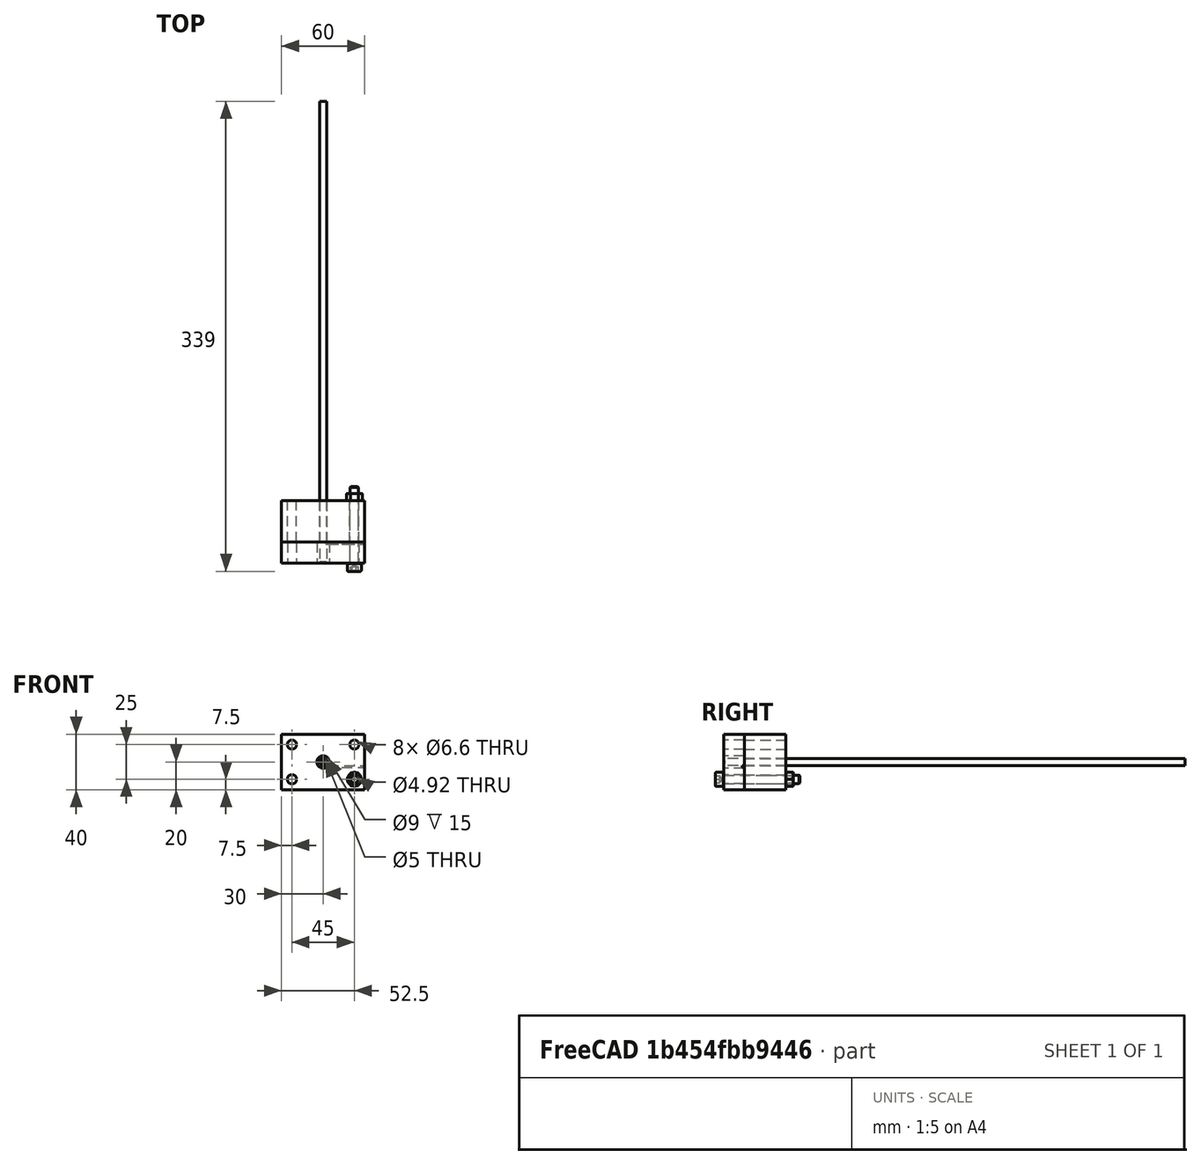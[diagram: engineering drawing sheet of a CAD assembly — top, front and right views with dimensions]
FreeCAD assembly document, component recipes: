
FREECAD ASSEMBLY — COMPONENT RECIPES ("coil winder")

This assembly document has 4 components, labeled P0..P3 below (a component is one placed body or linked part). 3 of them carry a construction recipe — the FreeCAD feature program that regenerates the part from scratch, quoted from this document or its linked companion documents; the rest are supplied as boundary geometry only. No exploded tour is included for this assembly.
COMPONENT P0 — geometry summary ("block fasteners"; no construction recipe available for this part):
  bounding box: 61.0 x 56.5 x 35.0 mm
  tessellated surface: 35,832 triangles
  volume: 9135 mm^3 (8% of its bounding box)
  symmetry: 2-fold rotationally symmetric about the y axis; mirror-symmetric across its x mid-plane, z mid-plane
COMPONENT P1 — recipe-attached ("OCT-CWFBL-AA", modeled in this document).
Construction recipe (the document's own serialized feature program — sketch geometry with constraints, then the solid features built on it; lengths are millimeters unless a unit is written):

FEATURE [PartDesign::SubShapeBinder] Binder  label="rear block binder"
  BindCopyOnChange = 0
  BindMode = 0
  ClaimChildren = false
  Context = -> Body001 [Binder.]
  Fuse = false
  MakeFace = true
  OffsetFill = false
  OffsetIntersection = false
  OffsetJoinType = 0
  OffsetOpenResult = false
  PartialLoad = false
  Refine = true
  Relative = true
  Support = -> [Body[Hole002.]]
  _Version = 2
FEATURE [Sketcher::SketchObject] Sketch002
  ArcFitTolerance = 1e-06
  AttachmentSupport = -> [XZ_Plane001]
  ExternalGeometry = -> [Binder]
  FullyConstrained = true
  MakeInternals = false
  MapMode = 5
  Placement = pos=(0,0,0) rot=(1,0,0;1.5708rad)
  sketch-geometry (4):
    g0: LineSegment StartX=-30 StartY=0 StartZ=0 EndX=30 EndY=0 EndZ=0
    g1: LineSegment StartX=30 StartY=0 StartZ=0 EndX=30 EndY=40 EndZ=0
    g2: LineSegment StartX=30 StartY=40 StartZ=0 EndX=-30 EndY=40 EndZ=0
    g3: LineSegment StartX=-30 StartY=40 StartZ=0 EndX=-30 EndY=0 EndZ=0
  constraints (10):
    c: Coincident(g0,g1)
    c: Coincident(g1,g2)
    c: Coincident(g2,g3)
    c: Coincident(g3,g0)
    c: Horizontal(g2)
    c: Vertical(g1)
    c: Vertical(g3)
    c: PointOnObject(g0,g-1)
    c: Coincident(g2,g-3)
    c: Symmetric(g0,g0,g-2)
FEATURE [PartDesign::Pad] Pad001
  Direction = (0,-1,2e-16)
  Length = 15
  Length2 = 10
  Placement = pos=(0,0,0) rot=(1,0,0;1.5708rad)
  Profile = -> Sketch002
  ReferenceAxis = -> Sketch002 [N_Axis]
  Refine = true
  Suppressed = false
  Type = 0
FEATURE [Sketcher::SketchObject] Sketch003
  ArcFitTolerance = 1e-06
  AttachmentSupport = -> [XZ_Plane001]
  ExternalGeometry = -> [Binder]
  FullyConstrained = true
  MakeInternals = false
  MapMode = 5
  Placement = pos=(0,0,0) rot=(1,0,0;1.5708rad)
  expr: Constraints[0] = <<dims>>.shaftDiameter + 2 * <<dims>>.wireDiameter
  sketch-geometry (1):
    g0: Circle CenterX=0 CenterY=20 CenterZ=0 NormalX=0 NormalY=0 NormalZ=1 AngleXU=0 Radius=3.52
  constraints (2):
    c: Diameter(g0) = 7.04
    c: Coincident(g0,g-3)
FEATURE [PartDesign::Hole] Hole001  label="coil bore"
  BaseFeature = -> Pad001
  CustomThreadClearance = 0
  Depth = 148.782
  DepthType = 1
  Diameter = 9
  DrillForDepth = false
  DrillPoint = 1
  DrillPointAngle = 118
  HoleCutCountersinkAngle = 90
  HoleCutCustomValues = false
  HoleCutDepth = 0
  HoleCutDiameter = 6.1
  HoleCutType = 0
  ModelThread = false
  Placement = pos=(0,0,0) rot=(1,0,0;1.5708rad)
  Profile = -> Sketch003
  Refine = true
  Reversed = true
  Suppressed = false
  Tapered = false
  TaperedAngle = 90
  ThreadClass = 0
  ThreadDepth = 148.782
  ThreadDepthType = 0
  ThreadDirection = 0
  ThreadFit = 0
  ThreadSize = 0
  ThreadType = 0
  Threaded = false
  UseCustomThreadClearance = false
  expr: Diameter = ceil(<<dims>>.shaftDiameter + 2 * <<dims>>.wireDiameter) + 1 mm
FEATURE [Sketcher::SketchObject] Sketch004
  ArcFitTolerance = 1e-06
  AttachmentSupport = -> [YZ_Plane001]
  ExternalGeometry = -> [Hole001]
  FullyConstrained = true
  MakeInternals = false
  MapMode = 5
  Placement = pos=(0,0,0) rot=(0.57735,0.57735,0.57735;2.0944rad)
  expr: Constraints[17] = <<dims>>.shaftDiameter / 2
  expr: Constraints[8] = <<dims>>.wireDiameter + 0.5 mm
  sketch-geometry (8):
    g0: LineSegment StartX=-1.52 StartY=15.98 StartZ=0 EndX=4e-15 EndY=15.98 EndZ=0
    g1: LineSegment StartX=4e-15 StartY=15.98 StartZ=0 EndX=4e-15 EndY=17.5 EndZ=0
    g2: LineSegment StartX=4e-15 StartY=17.5 StartZ=0 EndX=-1.52 EndY=17.5 EndZ=0
    g3: LineSegment StartX=-1.52 StartY=17.5 StartZ=0 EndX=-1.52 EndY=15.98 EndZ=0
    g4: LineSegment [constr] StartX=-1.52 StartY=17.5 StartZ=0 EndX=4e-15 EndY=15.98 EndZ=0
    g5: LineSegment [constr] StartX=-1.52 StartY=15.98 StartZ=0 EndX=4e-15 EndY=17.5 EndZ=0
    g6: GeomPoint [constr] X=-0.76 Y=16.74 Z=0
    g7: GeomPoint [constr] X=4.4e-15 Y=20 Z=0
  constraints (19):
    c: Coincident(g0,g1)
    c: Coincident(g1,g2)
    c: Coincident(g2,g3)
    c: Coincident(g3,g0)
    c: Horizontal(g0)
    c: Horizontal(g2)
    c: Vertical(g1)
    c: Vertical(g3)
    c: DistanceY(g3,g3) = 1.52
    c: Coincident(g4,g2)
    c: Coincident(g4,g0)
    c: Coincident(g5,g0)
    c: Coincident(g5,g1)
    c: PointOnObject(g6,g4)
    c: PointOnObject(g6,g5)
    c: Equal(g3,g0)
    c: Symmetric(g-3,g-3,g7)
    c: DistanceY(g1,g7) = 2.5
    c: PointOnObject(g1,g-3)
FEATURE [PartDesign::Pocket] Pocket  label="wire insert groove"
  BaseFeature = -> Hole001
  Direction = (-1,0,0)
  Length = 5
  Length2 = 5
  Placement = pos=(0,0,0) rot=(1,0,0;1.5708rad)
  Profile = -> Sketch004
  ReferenceAxis = -> Sketch004 [N_Axis]
  Refine = true
  Reversed = true
  Suppressed = false
  Type = 1
FEATURE [Sketcher::SketchObject] Sketch006
  ArcFitTolerance = 1e-06
  AttachmentSupport = -> [XZ_Plane001]
  FullyConstrained = true
  MakeInternals = false
  MapMode = 5
  Placement = pos=(0,0,0) rot=(1,0,0;1.5708rad)
  expr: Constraints[18] = <<dims>>.holeSpacingX
  expr: Constraints[19] = <<dims>>.holeSpacingZ
  expr: Constraints[20] = <<dims>>.shaftZ
  sketch-geometry (9):
    g0: LineSegment [constr] StartX=-22.5 StartY=7.5 StartZ=0 EndX=22.5 EndY=7.5 EndZ=0
    g1: LineSegment [constr] StartX=22.5 StartY=7.5 StartZ=0 EndX=22.5 EndY=32.5 EndZ=0
    g2: LineSegment [constr] StartX=22.5 StartY=32.5 StartZ=0 EndX=-22.5 EndY=32.5 EndZ=0
    g3: LineSegment [constr] StartX=-22.5 StartY=32.5 StartZ=0 EndX=-22.5 EndY=7.5 EndZ=0
    g4: GeomPoint [constr] X=0 Y=20 Z=0
    g5: Circle CenterX=-22.5 CenterY=32.5 CenterZ=0 NormalX=0 NormalY=0 NormalZ=1 AngleXU=0 Radius=3
    g6: Circle CenterX=22.5 CenterY=32.5 CenterZ=0 NormalX=0 NormalY=0 NormalZ=1 AngleXU=0 Radius=3
    g7: Circle CenterX=22.5 CenterY=7.5 CenterZ=0 NormalX=0 NormalY=0 NormalZ=1 AngleXU=0 Radius=3
    g8: Circle CenterX=-22.5 CenterY=7.5 CenterZ=0 NormalX=0 NormalY=0 NormalZ=1 AngleXU=0 Radius=3
  constraints (21):
    c: Coincident(g0,g1)
    c: Coincident(g1,g2)
    c: Coincident(g2,g3)
    c: Coincident(g3,g0)
    c: Horizontal(g0)
    c: Horizontal(g2)
    c: Vertical(g1)
    c: Vertical(g3)
    c: Symmetric(g2,g0,g4)
    c: PointOnObject(g4,g-2)
    c: Coincident(g5,g2)
    c: Coincident(g6,g1)
    c: Coincident(g7,g0)
    c: Coincident(g8,g0)
    c: Equal(g8,g5)
    c: Equal(g5,g6)
    c: Equal(g6,g7)
    c: Diameter(g5) = 6
    c: DistanceX(g2,g2) = 45
    c: DistanceY(g3,g3) = 25
    c: DistanceY(g-1,g4) = 20
FEATURE [PartDesign::Hole] Hole003  label="bolt holes"
  BaseFeature = -> Pocket
  CustomThreadClearance = 0
  Depth = 148.782
  DepthType = 1
  Diameter = 6.6
  DrillForDepth = false
  DrillPoint = 1
  DrillPointAngle = 118
  HoleCutCountersinkAngle = 90
  HoleCutCustomValues = false
  HoleCutDepth = 0
  HoleCutDiameter = 6.1
  HoleCutType = 0
  ModelThread = false
  Placement = pos=(0,0,0) rot=(1,0,0;1.5708rad)
  Profile = -> Sketch006
  Refine = true
  Reversed = true
  Suppressed = false
  Tapered = false
  TaperedAngle = 90
  ThreadClass = 0
  ThreadDepth = 148.782
  ThreadDepthType = 0
  ThreadDirection = 0
  ThreadFit = 0
  ThreadSize = 14
  ThreadType = 1
  Threaded = false
  UseCustomThreadClearance = false
FEATURE [PartDesign::Body] Body001  label="OCT-CWFBL-AA"
  AllowCompound = false
  Group = -> [Binder,Sketch002,Pad001,Sketch003,Hole001,Sketch004,Pocket,Sketch006,Hole003]
  Origin = -> Origin001
  Tip = -> Hole003
COMPONENT P2 — recipe-attached ("OCT-CWRBL-AA", modeled in this document).
Construction recipe (the document's own serialized feature program — sketch geometry with constraints, then the solid features built on it; lengths are millimeters unless a unit is written):

FEATURE [Sketcher::SketchObject] Sketch  label="block profile"
  ArcFitTolerance = 1e-06
  AttachmentSupport = -> [XZ_Plane]
  FullyConstrained = true
  MakeInternals = false
  MapMode = 5
  Placement = pos=(0,0,0) rot=(1,0,0;1.5708rad)
  expr: Constraints[11] = <<dims>>.shaftDiameter
  sketch-geometry (7):
    g0: LineSegment StartX=-30 StartY=0 StartZ=0 EndX=30 EndY=0 EndZ=0
    g1: LineSegment StartX=30 StartY=0 StartZ=0 EndX=30 EndY=40 EndZ=0
    g2: LineSegment StartX=30 StartY=40 StartZ=0 EndX=-30 EndY=40 EndZ=0
    g3: LineSegment StartX=-30 StartY=40 StartZ=0 EndX=-30 EndY=0 EndZ=0
    g4: Circle [constr] CenterX=0 CenterY=20 CenterZ=0 NormalX=0 NormalY=0 NormalZ=1 AngleXU=0 Radius=2.5
    g5: LineSegment [constr] StartX=2 StartY=18.5 StartZ=0 EndX=30 EndY=18.5 EndZ=0
    g6: GeomPoint [constr] X=0 Y=17.5 Z=0
  constraints (20):
    c: Coincident(g0,g1)
    c: Coincident(g1,g2)
    c: Coincident(g2,g3)
    c: Coincident(g3,g0)
    c: Horizontal(g2)
    c: Vertical(g1)
    c: Vertical(g3)
    c: PointOnObject(g0,g-1)
    c: PointOnObject(g4,g-2)
    c: PointOnObject(g5,g4)
    c: Horizontal(g5)
    c: Diameter(g4) = 5
    c: PointOnObject(g6,g4)
    c: PointOnObject(g6,g-2)
    c: DistanceY(g6,g5) = 1
    c: DistanceY(g-1,g4) = 20
    c: DistanceY(g3,g3) = 40
    c: DistanceX(g2,g2) = 60
    c: Symmetric(g0,g0,g-2)
    c: PointOnObject(g5,g1)
FEATURE [PartDesign::Pad] Pad
  Direction = (0,-1,2e-16)
  Length = 30
  Length2 = 10
  Placement = pos=(0,0,0) rot=(1,0,0;1.5708rad)
  Profile = -> Sketch
  ReferenceAxis = -> Sketch [N_Axis]
  Refine = true
  Reversed = true
  Suppressed = false
  Type = 0
FEATURE [Sketcher::SketchObject] Sketch001
  ArcFitTolerance = 1e-06
  AttachmentSupport = -> [XZ_Plane]
  FullyConstrained = true
  MakeInternals = false
  MapMode = 5
  Placement = pos=(0,0,0) rot=(1,0,0;1.5708rad)
  expr: Constraints[1] = <<dims>>.shaftDiameter
  expr: Constraints[2] = <<dims>>.shaftZ
  sketch-geometry (1):
    g0: Circle CenterX=0 CenterY=20 CenterZ=0 NormalX=0 NormalY=0 NormalZ=1 AngleXU=0 Radius=2.5
  constraints (3):
    c: PointOnObject(g0,g-2)
    c: Diameter(g0) = 5
    c: DistanceY(g-1,g0) = 20
FEATURE [PartDesign::Hole] Hole  label="shaft bore"
  BaseFeature = -> Pad
  CustomThreadClearance = 0
  Depth = 166.573
  DepthType = 1
  Diameter = 5
  DrillForDepth = false
  DrillPoint = 1
  DrillPointAngle = 118
  HoleCutCountersinkAngle = 90
  HoleCutCustomValues = false
  HoleCutDepth = 0
  HoleCutDiameter = 6.1
  HoleCutType = 0
  ModelThread = false
  Placement = pos=(0,0,0) rot=(1,0,0;1.5708rad)
  Profile = -> Sketch001
  Refine = true
  Suppressed = false
  Tapered = false
  TaperedAngle = 90
  ThreadClass = 0
  ThreadDepth = 166.573
  ThreadDepthType = 0
  ThreadDirection = 0
  ThreadFit = 0
  ThreadSize = 0
  ThreadType = 0
  Threaded = false
  UseCustomThreadClearance = false
  expr: Diameter = <<dims>>.shaftDiameter
FEATURE [Sketcher::SketchObject] Sketch005
  ArcFitTolerance = 1e-06
  AttachmentSupport = -> [XZ_Plane]
  ExternalGeometry = -> [Hole]
  FullyConstrained = true
  MakeInternals = false
  MapMode = 5
  Placement = pos=(0,0,0) rot=(1,0,0;1.5708rad)
  expr: Constraints[17] = <<dims>>.holeSpacingX
  expr: Constraints[18] = <<dims>>.holeSpacingZ
  sketch-geometry (9):
    g0: Circle CenterX=-22.5 CenterY=32.5 CenterZ=0 NormalX=0 NormalY=0 NormalZ=1 AngleXU=0 Radius=3
    g1: Circle CenterX=22.5 CenterY=7.5 CenterZ=0 NormalX=0 NormalY=0 NormalZ=1 AngleXU=0 Radius=3
    g2: Circle CenterX=22.5 CenterY=32.5 CenterZ=0 NormalX=0 NormalY=0 NormalZ=1 AngleXU=0 Radius=3
    g3: Circle CenterX=-22.5 CenterY=7.5 CenterZ=0 NormalX=0 NormalY=0 NormalZ=1 AngleXU=0 Radius=3
    g4: LineSegment [constr] StartX=-22.5 StartY=7.5 StartZ=0 EndX=22.5 EndY=7.5 EndZ=0
    g5: LineSegment [constr] StartX=22.5 StartY=7.5 StartZ=0 EndX=22.5 EndY=32.5 EndZ=0
    g6: LineSegment [constr] StartX=22.5 StartY=32.5 StartZ=0 EndX=-22.5 EndY=32.5 EndZ=0
    g7: LineSegment [constr] StartX=-22.5 StartY=32.5 StartZ=0 EndX=-22.5 EndY=7.5 EndZ=0
    g8: GeomPoint [constr] X=-1e-16 Y=20 Z=0
  constraints (20):
    c: Equal(g0,g2)
    c: Equal(g2,g1)
    c: Equal(g1,g3)
    c: Coincident(g4,g5)
    c: Coincident(g5,g6)
    c: Coincident(g6,g7)
    c: Coincident(g7,g4)
    c: Horizontal(g4)
    c: Horizontal(g6)
    c: Vertical(g5)
    c: Vertical(g7)
    c: Symmetric(g6,g4,g8)
    c: Coincident(g8,g-3)
    c: Coincident(g5,g2)
    c: Coincident(g4,g3)
    c: Coincident(g0,g6)
    c: Coincident(g1,g4)
    c: DistanceX(g6,g6) = 45
    c: DistanceY(g7,g7) = 25
    c: Diameter(g0) = 6
FEATURE [PartDesign::Hole] Hole002  label="bolt holes"
  BaseFeature = -> Hole
  CustomThreadClearance = 0
  Depth = 166.573
  DepthType = 1
  Diameter = 6.6
  DrillForDepth = false
  DrillPoint = 1
  DrillPointAngle = 118
  HoleCutCountersinkAngle = 90
  HoleCutCustomValues = false
  HoleCutDepth = 0
  HoleCutDiameter = 0
  HoleCutType = 0
  ModelThread = false
  Placement = pos=(0,0,0) rot=(1,0,0;1.5708rad)
  Profile = -> Sketch005
  Refine = true
  Suppressed = false
  Tapered = false
  TaperedAngle = 90
  ThreadClass = 0
  ThreadDepth = 166.573
  ThreadDepthType = 0
  ThreadDirection = 0
  ThreadFit = 0
  ThreadSize = 14
  ThreadType = 1
  Threaded = false
  UseCustomThreadClearance = false
FEATURE [PartDesign::Body] Body  label="OCT-CWRBL-AA"
  AllowCompound = false
  Group = -> [Sketch,Pad,Sketch001,Hole,Sketch005,Hole002]
  Origin = -> Origin
  Tip = -> Hole002
COMPONENT P3 — recipe-attached ("OCT-CWSFT-AA", modeled in this document).
Construction recipe (the document's own serialized feature program — sketch geometry with constraints, then the solid features built on it; lengths are millimeters unless a unit is written):

FEATURE [PartDesign::SubShapeBinder] Binder001
  BindCopyOnChange = 0
  BindMode = 0
  ClaimChildren = false
  Context = -> Body002 [Binder001.]
  Fuse = false
  MakeFace = true
  OffsetFill = false
  OffsetIntersection = false
  OffsetJoinType = 0
  OffsetOpenResult = false
  PartialLoad = false
  Refine = true
  Relative = true
  Support = -> [Body[Hole002.Face5],Body001[Hole003.Face5]]
  _Version = 2
FEATURE [Sketcher::SketchObject] Sketch007
  ArcFitTolerance = 1e-06
  AttachmentSupport = -> [YZ_Plane002]
  ExternalGeometry = -> [Binder001]
  FullyConstrained = true
  MakeInternals = false
  MapMode = 5
  Placement = pos=(0,0,0) rot=(0.57735,0.57735,0.57735;2.0944rad)
  expr: Constraints[8] = <<dims>>.shaftZ
  expr: Constraints[9] = <<dims>>.shaftDiameter / 2
  sketch-geometry (4):
    g0: LineSegment StartX=-15 StartY=20 StartZ=0 EndX=318 EndY=20 EndZ=0
    g1: LineSegment StartX=318 StartY=20 StartZ=0 EndX=318 EndY=22.5 EndZ=0
    g2: LineSegment StartX=318 StartY=22.5 StartZ=0 EndX=-15 EndY=22.5 EndZ=0
    g3: LineSegment StartX=-15 StartY=22.5 StartZ=0 EndX=-15 EndY=20 EndZ=0
  constraints (12):
    c: Coincident(g0,g1)
    c: Coincident(g1,g2)
    c: Coincident(g2,g3)
    c: Coincident(g3,g0)
    c: Horizontal(g0)
    c: Horizontal(g2)
    c: Vertical(g1)
    c: Vertical(g3)
    c: DistanceY(g-1,g0) = 20
    c: DistanceY(g3,g3) = 2.5
    c: Vertical(g2,g-3)
    c: DistanceX(g2,g2) = 333
FEATURE [PartDesign::Revolution] Revolution
  Angle = 360
  Angle2 = 60
  Axis = (0,1,0)
  Base = (0,-15,20)
  Placement = pos=(0,0,0) rot=(1,1,1;2.0944rad)
  Profile = -> Sketch007
  ReferenceAxis = -> Sketch007 [Edge1]
  Refine = true
  Reversed = true
  Suppressed = false
  Type = 0
FEATURE [Sketcher::SketchObject] Sketch008
  ArcFitTolerance = 1e-06
  AttachmentSupport = -> [YZ_Plane002]
  ExternalGeometry = -> [Binder001]
  FullyConstrained = true
  MakeInternals = false
  MapMode = 5
  Placement = pos=(0,0,0) rot=(0.57735,0.57735,0.57735;2.0944rad)
  expr: Constraints[11] = <<dims>>.shaftZ
  expr: Constraints[8] = <<dims>>.wireDiameter + 1 mm
  expr: Constraints[9] = <<dims>>.wireDiameter
  sketch-geometry (5):
    g0: LineSegment StartX=-15 StartY=21.01 StartZ=0 EndX=-15 EndY=18.99 EndZ=0
    g1: LineSegment StartX=-15 StartY=18.99 StartZ=0 EndX=-13.98 EndY=18.99 EndZ=0
    g2: LineSegment StartX=-13.98 StartY=18.99 StartZ=0 EndX=-13.98 EndY=21.01 EndZ=0
    g3: LineSegment StartX=-13.98 StartY=21.01 StartZ=0 EndX=-15 EndY=21.01 EndZ=0
    g4: GeomPoint X=-15 Y=20 Z=0
  constraints (13):
    c: Coincident(g0,g1)
    c: Coincident(g1,g2)
    c: Coincident(g2,g3)
    c: Coincident(g3,g0)
    c: Vertical(g0)
    c: Vertical(g2)
    c: Horizontal(g1)
    c: Horizontal(g3)
    c: DistanceY(g0,g0) = 2.02
    c: DistanceX(g1,g1) = 1.02
    c: Symmetric(g0,g0,g4)
    c: DistanceY(g-1,g4) = 20
    c: Vertical(g0,g-3)
FEATURE [PartDesign::Pocket] Pocket001
  BaseFeature = -> Revolution
  Direction = (-1,0,0)
  Length = 5
  Length2 = 5
  Midplane = true
  Placement = pos=(0,0,0) rot=(1,1,1;2.0944rad)
  Profile = -> Sketch008
  ReferenceAxis = -> Sketch008 [N_Axis]
  Refine = true
  Suppressed = false
  Type = 1
FEATURE [PartDesign::Body] Body002  label="OCT-CWSFT-AA"
  AllowCompound = false
  Group = -> [Binder001,Sketch007,Revolution,Sketch008,Pocket001]
  Origin = -> Origin002
  Tip = -> Pocket001
PROVENANCE & LICENSES
A FreeCAD (.FCStd) document from a public repository crawl; recipes are the document's own serialized feature recipes (and, for linked parts, companion documents' recipes).
License: mit.
